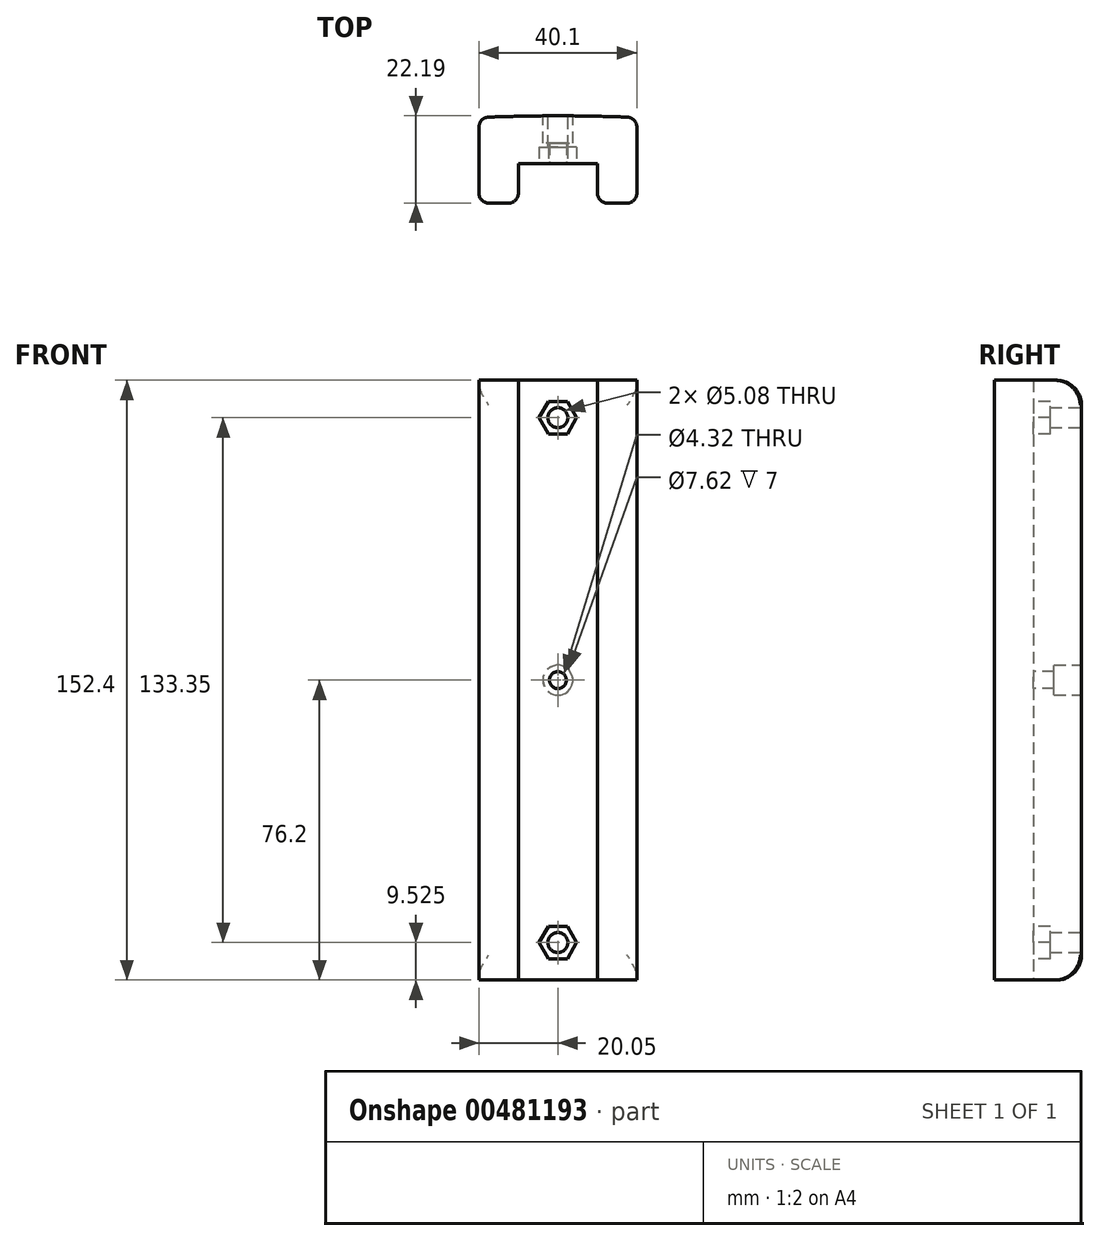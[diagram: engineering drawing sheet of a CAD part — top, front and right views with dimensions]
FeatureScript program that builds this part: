
annotation { "Feature Type Name" : "Feature", "Feature Type Description" : "" }
export const myFeature = defineFeature(function(context is Context, id is Id, definition is map)
    precondition{}
    {
        {
            var Q0;
            Q0=qCreatedBy(makeId("Top.planeOp"),FACE);
            var sketch = newSketch(context, id + "F0", { "sketchPlane" : qUnion([Q0])});
            skLineSegment(sketch, "E0", {"start": v(0, 0) * mm, "end": v(10.05, 0) * mm, "construction": true});
            skLineSegment(sketch, "E1", {"start": v(10.05, 0) * mm, "end": v(0, 0) * mm});
            skLineSegment(sketch, "E2", {"start": v(10.05, 0) * mm, "end": v(10.05, -10) * mm});
            skLineSegment(sketch, "E3", {"start": v(10.05, -10) * mm, "end": v(20.05, -10) * mm});
            skLineSegment(sketch, "E4", {"start": v(0, 0) * mm, "end": v(0, 6.02) * mm, "construction": true});
            skLineSegment(sketch, "E5.MirrorCS", {"start": v(-10.05, 0) * mm, "end": v(0, 0) * mm});
            skLineSegment(sketch, "E6.MirrorCS", {"start": v(-10.05, 0) * mm, "end": v(-10.05, -10) * mm});
            skLineSegment(sketch, "E7.MirrorCS", {"start": v(-10.05, -10) * mm, "end": v(-20.05, -10) * mm});
            skLineSegment(sketch, "E8", {"start": v(0, 0) * mm, "end": v(0, 12.2) * mm, "construction": true});
            skLineSegment(sketch, "E9", {"start": v(0, 12.2) * mm, "end": v(0, 63) * mm, "construction": true});
            skLineSegment(sketch, "E10", {"start": v(-20.05, -10) * mm, "end": v(-20.05, 11.8) * mm});
            skLineSegment(sketch, "E11", {"start": v(20.05, -10) * mm, "end": v(20.05, 11.8) * mm});
            skFitSpline(sketch, "E12", {"points": [v(-20.05, 11.8) * mm, v(0, 12.2) * mm, v(20.05, 11.8) * mm], "startDerivative": vector(40.1, 1.19) * mm, "endDerivative": vector(40.1, -1.19) * mm});
            skLineSegment(sketch, "E13", {"start": v(20.05, 11.8) * mm, "end": v(20.05, 62.12) * mm});
            skLineSegment(sketch, "E14.MirrorCS", {"start": v(-20.05, 11.8) * mm, "end": v(-20.05, 62.12) * mm});
            skFitSpline(sketch, "E15", {"points": [v(-20.05, 62.12) * mm, v(0, 63) * mm, v(20.05, 62.12) * mm], "startDerivative": vector(40.1, 2.62) * mm, "endDerivative": vector(40.1, -2.62) * mm});
            skLineSegment(sketch, "E16", {"start": v(-20.05, 36.96) * mm, "end": v(20.05, 36.96) * mm, "construction": true});
            skSolve(sketch);
        }
        {
            var Q0;
            Q0=makeQuery(id+"F0.imprint","IMPRINT",FACE,{"disambiguationData":[TD([[makeQuery(id+"F0.imprint","IMPRINT",EDGE,{"derivedFrom":sQuery(id+"F0.wireOp",EDGE,"E1")}),-1.0]])]});
            extrude(context, id + "F1", {"entities" : qUnion([Q0]), "depth" : 152.4 * mm});
        }
        {
            var Q0;
            Q0=makeQuery(id+"F1.opExtrude","SWEPT_EDGE",EDGE,{"disambiguationData":[OSD([sQuery(id+"F0.wireOp",EDGE,"E11"),sQuery(id+"F0.wireOp",EDGE,"E12"),sQuery(id+"F0.wireOp",EDGE,"E13")])]});
            var Q1;
            Q1=makeQuery(id+"F1.opExtrude","SWEPT_EDGE",EDGE,{"disambiguationData":[OSD([sQuery(id+"F0.wireOp",EDGE,"E10"),sQuery(id+"F0.wireOp",EDGE,"E12"),sQuery(id+"F0.wireOp",EDGE,"E14.MirrorCS")])]});
            fillet(context, id + "F2", {"entities" : qUnion([Q0, Q1]), "radius" : 2.54 * mm, "tangentPropagation" : true, "allowEdgeOverflow" : false});
        }
        {
            var Q0;
            Q0=makeQuery(id+"F1.opExtrude","CAP_EDGE",EDGE,{"disambiguationData":[OSD([sQuery(id+"F0.wireOp",EDGE,"E12")])],"isStart":true});
            var Q1;
            {var subQ0=sQuery(id+"F0.wireOp",EDGE,"E12");var subQ1=sQuery(id+"F0.wireOp",EDGE,"E11");Q1=makeQuery(id+"F2.opFillet","BLEND_EDGE",EDGE,{"blendedFrom":[makeQuery(id+"F1.opExtrude","SWEPT_EDGE",EDGE,{"disambiguationData":[OSD([subQ1,subQ0,sQuery(id+"F0.wireOp",EDGE,"E13")])]}),makeQuery(id+"F1.opExtrude","CAP_FACE",FACE,{"disambiguationData":[OSD([sQuery(id+"F0.wireOp",EDGE,"E1"),sQuery(id+"F0.wireOp",EDGE,"E2"),sQuery(id+"F0.wireOp",EDGE,"E3"),sQuery(id+"F0.wireOp",EDGE,"E5.MirrorCS"),sQuery(id+"F0.wireOp",EDGE,"E6.MirrorCS"),sQuery(id+"F0.wireOp",EDGE,"E7.MirrorCS"),sQuery(id+"F0.wireOp",EDGE,"E10"),subQ1,subQ0])],"isStart":true})],"blendedInto":[makeQuery(id+"F1.opExtrude","CAP_FACE",FACE,{"disambiguationData":[OSD([sQuery(id+"F0.wireOp",EDGE,"E1"),sQuery(id+"F0.wireOp",EDGE,"E2"),sQuery(id+"F0.wireOp",EDGE,"E3"),sQuery(id+"F0.wireOp",EDGE,"E5.MirrorCS"),sQuery(id+"F0.wireOp",EDGE,"E6.MirrorCS"),sQuery(id+"F0.wireOp",EDGE,"E7.MirrorCS"),sQuery(id+"F0.wireOp",EDGE,"E10"),subQ1,subQ0])],"isStart":true})]});}
            var Q2;
            {var subQ0=sQuery(id+"F0.wireOp",EDGE,"E12");var subQ1=sQuery(id+"F0.wireOp",EDGE,"E10");Q2=makeQuery(id+"F2.opFillet","BLEND_EDGE",EDGE,{"blendedFrom":[makeQuery(id+"F1.opExtrude","SWEPT_EDGE",EDGE,{"disambiguationData":[OSD([subQ1,subQ0,sQuery(id+"F0.wireOp",EDGE,"E14.MirrorCS")])]}),makeQuery(id+"F1.opExtrude","CAP_FACE",FACE,{"disambiguationData":[OSD([sQuery(id+"F0.wireOp",EDGE,"E1"),sQuery(id+"F0.wireOp",EDGE,"E2"),sQuery(id+"F0.wireOp",EDGE,"E3"),sQuery(id+"F0.wireOp",EDGE,"E5.MirrorCS"),sQuery(id+"F0.wireOp",EDGE,"E6.MirrorCS"),sQuery(id+"F0.wireOp",EDGE,"E7.MirrorCS"),subQ1,sQuery(id+"F0.wireOp",EDGE,"E11"),subQ0])],"isStart":true})],"blendedInto":[makeQuery(id+"F1.opExtrude","CAP_FACE",FACE,{"disambiguationData":[OSD([sQuery(id+"F0.wireOp",EDGE,"E1"),sQuery(id+"F0.wireOp",EDGE,"E2"),sQuery(id+"F0.wireOp",EDGE,"E3"),sQuery(id+"F0.wireOp",EDGE,"E5.MirrorCS"),sQuery(id+"F0.wireOp",EDGE,"E6.MirrorCS"),sQuery(id+"F0.wireOp",EDGE,"E7.MirrorCS"),subQ1,sQuery(id+"F0.wireOp",EDGE,"E11"),subQ0])],"isStart":true})]});}
            var Q3;
            {var subQ0=sQuery(id+"F0.wireOp",EDGE,"E12");var subQ1=sQuery(id+"F0.wireOp",EDGE,"E10");Q3=makeQuery(id+"F2.opFillet","BLEND_EDGE",EDGE,{"blendedFrom":[makeQuery(id+"F1.opExtrude","SWEPT_EDGE",EDGE,{"disambiguationData":[OSD([subQ1,subQ0,sQuery(id+"F0.wireOp",EDGE,"E14.MirrorCS")])]}),makeQuery(id+"F1.opExtrude","CAP_FACE",FACE,{"disambiguationData":[OSD([sQuery(id+"F0.wireOp",EDGE,"E1"),sQuery(id+"F0.wireOp",EDGE,"E2"),sQuery(id+"F0.wireOp",EDGE,"E3"),sQuery(id+"F0.wireOp",EDGE,"E5.MirrorCS"),sQuery(id+"F0.wireOp",EDGE,"E6.MirrorCS"),sQuery(id+"F0.wireOp",EDGE,"E7.MirrorCS"),subQ1,sQuery(id+"F0.wireOp",EDGE,"E11"),subQ0])],"isStart":false})],"blendedInto":[makeQuery(id+"F1.opExtrude","CAP_FACE",FACE,{"disambiguationData":[OSD([sQuery(id+"F0.wireOp",EDGE,"E1"),sQuery(id+"F0.wireOp",EDGE,"E2"),sQuery(id+"F0.wireOp",EDGE,"E3"),sQuery(id+"F0.wireOp",EDGE,"E5.MirrorCS"),sQuery(id+"F0.wireOp",EDGE,"E6.MirrorCS"),sQuery(id+"F0.wireOp",EDGE,"E7.MirrorCS"),subQ1,sQuery(id+"F0.wireOp",EDGE,"E11"),subQ0])],"isStart":false})]});}
            var Q4;
            {var subQ0=sQuery(id+"F0.wireOp",EDGE,"E12");var subQ1=sQuery(id+"F0.wireOp",EDGE,"E11");Q4=makeQuery(id+"F2.opFillet","BLEND_EDGE",EDGE,{"blendedFrom":[makeQuery(id+"F1.opExtrude","SWEPT_EDGE",EDGE,{"disambiguationData":[OSD([subQ1,subQ0,sQuery(id+"F0.wireOp",EDGE,"E13")])]}),makeQuery(id+"F1.opExtrude","CAP_FACE",FACE,{"disambiguationData":[OSD([sQuery(id+"F0.wireOp",EDGE,"E1"),sQuery(id+"F0.wireOp",EDGE,"E2"),sQuery(id+"F0.wireOp",EDGE,"E3"),sQuery(id+"F0.wireOp",EDGE,"E5.MirrorCS"),sQuery(id+"F0.wireOp",EDGE,"E6.MirrorCS"),sQuery(id+"F0.wireOp",EDGE,"E7.MirrorCS"),sQuery(id+"F0.wireOp",EDGE,"E10"),subQ1,subQ0])],"isStart":false})],"blendedInto":[makeQuery(id+"F1.opExtrude","CAP_FACE",FACE,{"disambiguationData":[OSD([sQuery(id+"F0.wireOp",EDGE,"E1"),sQuery(id+"F0.wireOp",EDGE,"E2"),sQuery(id+"F0.wireOp",EDGE,"E3"),sQuery(id+"F0.wireOp",EDGE,"E5.MirrorCS"),sQuery(id+"F0.wireOp",EDGE,"E6.MirrorCS"),sQuery(id+"F0.wireOp",EDGE,"E7.MirrorCS"),sQuery(id+"F0.wireOp",EDGE,"E10"),subQ1,subQ0])],"isStart":false})]});}
            var Q5;
            Q5=makeQuery(id+"F1.opExtrude","CAP_EDGE",EDGE,{"disambiguationData":[OSD([sQuery(id+"F0.wireOp",EDGE,"E12")])],"isStart":false});
            fillet(context, id + "F3", {"entities" : qUnion([Q0, Q1, Q2, Q3, Q4, Q5]), "radius" : 6.35 * mm, "allowEdgeOverflow" : false});
        }
        {
            var Q0;
            Q0=makeQuery(id+"F1.opExtrude","SWEPT_EDGE",EDGE,{"disambiguationData":[OSD([sQuery(id+"F0.wireOp",EDGE,"E3"),sQuery(id+"F0.wireOp",EDGE,"E11")])]});
            var Q1;
            Q1=makeQuery(id+"F1.opExtrude","SWEPT_EDGE",EDGE,{"disambiguationData":[OSD([sQuery(id+"F0.wireOp",EDGE,"E2"),sQuery(id+"F0.wireOp",EDGE,"E3")])]});
            var Q2;
            Q2=makeQuery(id+"F1.opExtrude","SWEPT_EDGE",EDGE,{"disambiguationData":[OSD([sQuery(id+"F0.wireOp",EDGE,"E6.MirrorCS"),sQuery(id+"F0.wireOp",EDGE,"E7.MirrorCS")])]});
            var Q3;
            Q3=makeQuery(id+"F1.opExtrude","SWEPT_EDGE",EDGE,{"disambiguationData":[OSD([sQuery(id+"F0.wireOp",EDGE,"E7.MirrorCS"),sQuery(id+"F0.wireOp",EDGE,"E10")])]});
            fillet(context, id + "F4", {"entities" : qUnion([Q0, Q1, Q2, Q3]), "radius" : 2.54 * mm, "tangentPropagation" : true, "allowEdgeOverflow" : false});
        }
        {
            var Q0;
            Q0=makeQuery(id+"F1.opExtrude","SWEPT_FACE",FACE,{"disambiguationData":[OSD([sQuery(id+"F0.wireOp",EDGE,"E1"),sQuery(id+"F0.wireOp",EDGE,"E5.MirrorCS")])]});
            var sketch = newSketch(context, id + "F5", { "sketchPlane" : qUnion([Q0])});
            skLineSegment(sketch, "E17", {"start": v(0, 0) * mm, "end": v(0, 76.2) * mm, "construction": true});
            skCircle(sketch, "E18", {"center": v(0, 76.2) * mm, "radius": 2.16 * mm});
            skSolve(sketch);
        }
        {
            var Q0;
            Q0=makeQuery(id+"F5.imprint","IMPRINT",FACE,{"disambiguationData":[TD([[makeQuery(id+"F5.imprint","IMPRINT",EDGE,{"derivedFrom":sQuery(id+"F5.wireOp",EDGE,"E18")}),1.0]])]});
            extrude(context, id + "F6", {"entities" : qUnion([Q0]), "operationType" : NewBodyOperationType.REMOVE, "oppositeDirection" : true, "depth" : 12.7 * mm});
        }
        {
            var Q0;
            Q0=qCreatedBy(makeId("Front.planeOp"),FACE);
            cPlane(context, id + "F7", {"entities" : qUnion([Q0]), "cplaneType" : CPlaneType.OFFSET, "offset" : 12.2 * mm, "oppositeDirection" : true, "width" : 152.4 * mm, "height" : 152.4 * mm});
        }
        {
            var Q0;
            Q0=qCreatedBy(id+"F7.planeOp",FACE);
            var sketch = newSketch(context, id + "F8", { "sketchPlane" : qUnion([Q0])});
            skLineSegment(sketch, "E19", {"start": v(0, 0) * mm, "end": v(0, 76.2) * mm, "construction": true});
            skCircle(sketch, "E20", {"center": v(0, 76.2) * mm, "radius": 3.81 * mm});
            skSolve(sketch);
        }
        {
            var Q0;
            Q0=makeQuery(id+"F8.imprint","IMPRINT",FACE,{"disambiguationData":[TD([[makeQuery(id+"F8.imprint","IMPRINT",EDGE,{"derivedFrom":sQuery(id+"F8.wireOp",EDGE,"E20")}),1.0]])]});
            extrude(context, id + "F9", {"entities" : qUnion([Q0]), "operationType" : NewBodyOperationType.REMOVE, "depth" : 7 * mm});
        }
        {
            var Q0;
            Q0=qCreatedBy(id+"F7.planeOp",FACE);
            var sketch = newSketch(context, id + "F10", { "sketchPlane" : qUnion([Q0])});
            skPoint(sketch, "E21", {"position": v(0, 76.2) * mm});
            skLineSegment(sketch, "E22", {"start": v(0, 76.2) * mm, "end": v(0, 9.52) * mm, "construction": true});
            skCircle(sketch, "E23", {"center": v(0, 9.52) * mm, "radius": 2.54 * mm});
            skLineSegment(sketch, "E24", {"start": v(0, 76.2) * mm, "end": v(-7.62, 76.2) * mm, "construction": true});
            skCircle(sketch, "E25.MirrorC", {"center": v(0, 142.88) * mm, "radius": 2.54 * mm});
            skSolve(sketch);
        }
        {
            var Q0;
            Q0 = qSketchRegion(id + "F10", true);
            extrude(context, id + "F11", {"entities" : qUnion([Q0]), "operationType" : NewBodyOperationType.REMOVE, "depth" : 12.7 * mm});
        }
        {
            var Q0;
            Q0=makeQuery(id+"F1.opExtrude","SWEPT_FACE",FACE,{"disambiguationData":[OSD([sQuery(id+"F0.wireOp",EDGE,"E1"),sQuery(id+"F0.wireOp",EDGE,"E5.MirrorCS")])]});
            var sketch = newSketch(context, id + "F12", { "sketchPlane" : qUnion([Q0])});
            skCircle(sketch, "E26.cCircle", {"center": v(0, 9.52) * mm, "radius": 4.12 * mm, "construction": true});
            skLineSegment(sketch, "E26.0", {"start": v(-2.38, 13.65) * mm, "end": v(2.38, 13.65) * mm});
            skLineSegment(sketch, "E26.1", {"start": v(2.38, 13.65) * mm, "end": v(4.76, 9.52) * mm});
            skLineSegment(sketch, "E26.2", {"start": v(4.76, 9.52) * mm, "end": v(2.38, 5.4) * mm});
            skLineSegment(sketch, "E26.3", {"start": v(2.38, 5.4) * mm, "end": v(-2.38, 5.4) * mm});
            skLineSegment(sketch, "E26.4", {"start": v(-2.38, 5.4) * mm, "end": v(-4.76, 9.52) * mm});
            skLineSegment(sketch, "E26.5", {"start": v(-4.76, 9.52) * mm, "end": v(-2.38, 13.65) * mm});
            skPoint(sketch, "E26.0.midPoint", {"position": v(0, 13.65) * mm});
            skLineSegment(sketch, "E27", {"start": v(0, 76.2) * mm, "end": v(8.38, 76.2) * mm, "construction": true});
            skLineSegment(sketch, "E28.MirrorCS", {"start": v(4.76, 142.88) * mm, "end": v(2.38, 147) * mm});
            skLineSegment(sketch, "E29.MirrorCS", {"start": v(2.38, 147) * mm, "end": v(-2.38, 147) * mm});
            skLineSegment(sketch, "E30.MirrorCS", {"start": v(-2.38, 147) * mm, "end": v(-4.76, 142.88) * mm});
            skLineSegment(sketch, "E31.MirrorCS", {"start": v(-4.76, 142.88) * mm, "end": v(-2.38, 138.75) * mm});
            skLineSegment(sketch, "E32.MirrorCS", {"start": v(-2.38, 138.75) * mm, "end": v(2.38, 138.75) * mm});
            skLineSegment(sketch, "E33.MirrorCS", {"start": v(2.38, 138.75) * mm, "end": v(4.76, 142.88) * mm});
            skSolve(sketch);
        }
        {
            var Q0;
            Q0 = qSketchRegion(id + "F12", true);
            extrude(context, id + "F13", {"entities" : qUnion([Q0]), "operationType" : NewBodyOperationType.REMOVE, "oppositeDirection" : true, "depth" : 4.25 * mm});
        }
    });
